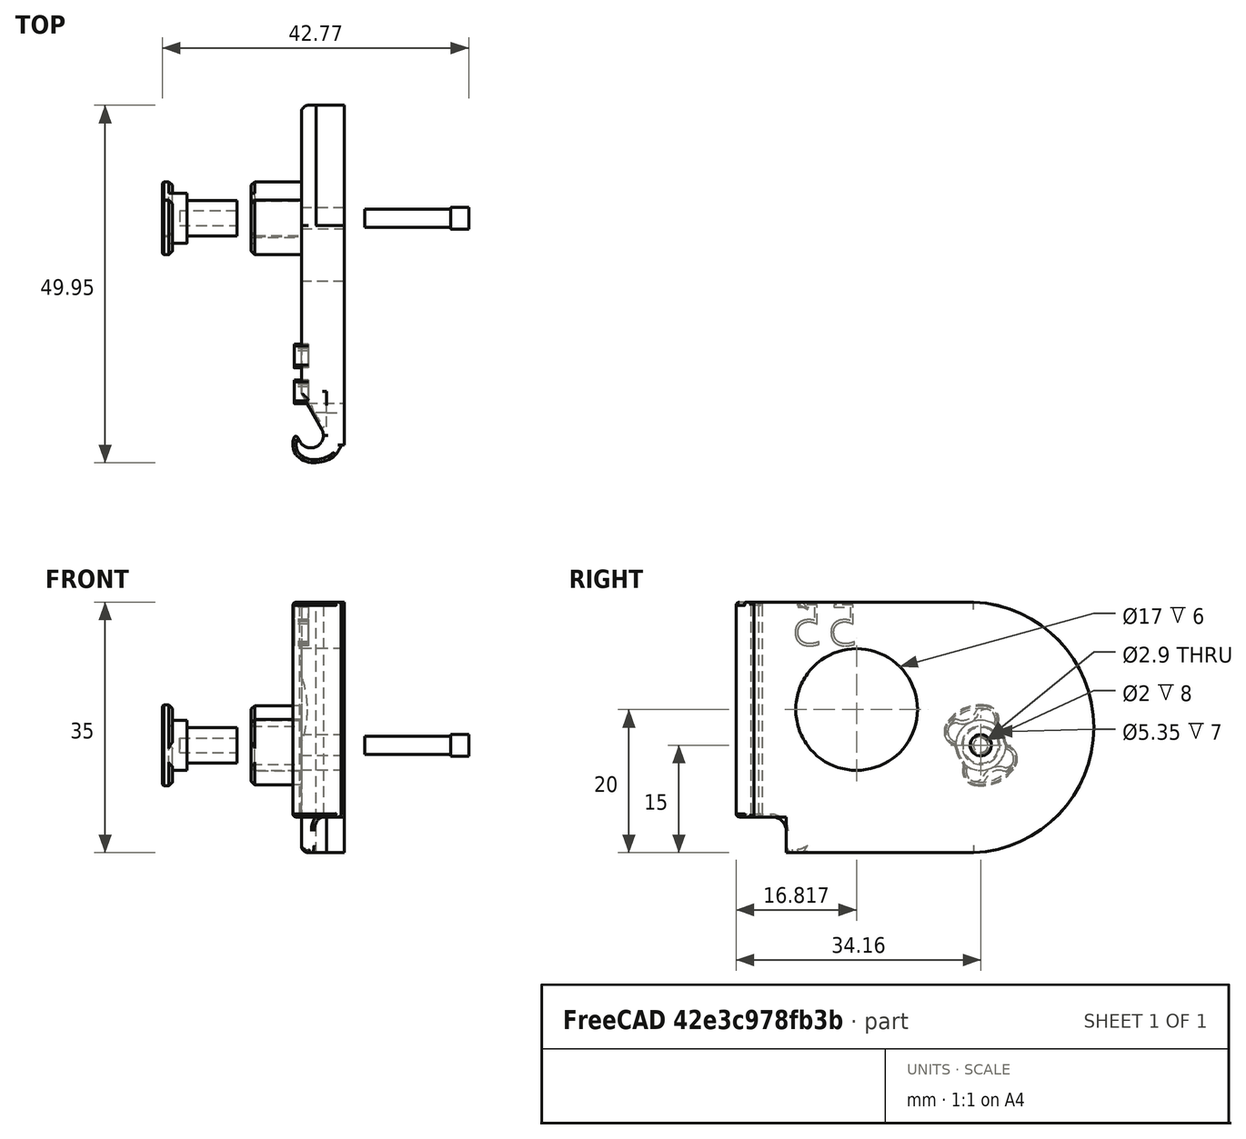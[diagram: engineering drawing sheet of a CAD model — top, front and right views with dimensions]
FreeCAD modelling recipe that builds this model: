
FCSTD DOCUMENT  (FreeCAD 0.18R)
Label: hinge-left-155deg-flat-measurements
License: All rights reserved
LicenseURL: http://en.wikipedia.org/wiki/All_rights_reserved
objects: App::FeaturePython×10, Part::FeaturePython×4, Part::Part2DObjectPython×1, Part::Extrusion×1
note: 6 computed .brp shape members not serialized (recipe doc carries the construction recipe); baked Part::Feature solids carry a one-line shape summary decoded from their .brp

FEATURE [Part::FeaturePython] pillar_base_001  label="pillar-base_001"  # a2plus imported part (geometry in sourceFile) (typed FeaturePython)
  Placement = pos=(0.000603061,0.00261841,-0.00477498) rot=(1,0,0;0.000175rad)
  a2p_Version = V0.1
  fixedPosition = true
  objectType = a2pPart
  sourceFile = ./parts/pillar-base.fcstd
  subassemblyImport = false
  timeLastImport = 1.60452e+09
  updateColors = true
FEATURE [Part::Part2DObjectPython] ShapeString  # Draft 2D object (typed FeaturePython)
  FontFile = <path>
  Placement = pos=(1.61,10.5,29) rot=(0.57735,-0.57735,-0.57735;2.0944rad)
  Size = 6
  String = 55
  Tracking = 0
FEATURE [Part::Extrusion] Extrude
  Base = -> ShapeString
  Dir = (-1,-1e-16,2e-16)
  DirMode = 2
  FaceMakerClass = Part::FaceMakerBullseye
  LengthFwd = 2
  LengthRev = 0
  Solid = false
  Symmetric = false
FEATURE [Part::FeaturePython] bracket_left_flat_001  label="bracket-left-flat_001"  # a2plus imported part (geometry in sourceFile) (typed FeaturePython)
  a2p_Version = V0.1
  fixedPosition = true
  objectType = a2pPart
  sourceFile = ./parts/bracket-left-flat.fcstd
  subassemblyImport = false
  timeLastImport = 1.60454e+09
  updateColors = true
FEATURE [App::FeaturePython] axisCoincident_001  label="axisCoincident_001__bracket-left-flat_001"  # a2plus constraint (typed FeaturePython)
  Object1 = pillar_base_001
  Object2 = bracket_left_flat_001
  ParentTreeObject = -> pillar_base_001
  SubElement1 = Face17
  SubElement2 = Face48
  Suppressed = false
  Type = axial
  directionConstraint = 1
  lockRotation = false
FEATURE [App::FeaturePython] axisCoincident_001_mirror  label="axisCoincident_001__pillar-base_001"  # a2plus constraint (typed FeaturePython)
  Object1 = pillar_base_001
  Object2 = bracket_left_flat_001
  ParentTreeObject = -> bracket_left_flat_001
  SubElement1 = Face17
  SubElement2 = Face48
  Suppressed = false
  Type = axial
  directionConstraint = 1
  lockRotation = false
FEATURE [App::FeaturePython] planeCoincident_001  label="planeCoincident_001__bracket-left-flat_001"  # a2plus constraint (typed FeaturePython)
  Object1 = pillar_base_001
  Object2 = bracket_left_flat_001
  ParentTreeObject = -> pillar_base_001
  SubElement1 = Face1
  SubElement2 = Face72
  Suppressed = false
  Type = plane
  directionConstraint = 0
  offset = 0
FEATURE [App::FeaturePython] planeCoincident_001_mirror  label="planeCoincident_001__pillar-base_001"  # a2plus constraint (typed FeaturePython)
  Object1 = pillar_base_001
  Object2 = bracket_left_flat_001
  ParentTreeObject = -> bracket_left_flat_001
  SubElement1 = Face1
  SubElement2 = Face72
  Suppressed = false
  Type = plane
  directionConstraint = 0
  offset = 0
FEATURE [Part::FeaturePython] pillar_post_001  label="pillar-post_001"  # a2plus imported part (geometry in sourceFile) (typed FeaturePython)
  Placement = pos=(-8.9994,1.6285e-12,-8.2e-15) rot=(0,0,1;0rad)
  a2p_Version = V0.1
  fixedPosition = false
  objectType = a2pPart
  sourceFile = ./parts/pillar-post.fcstd
  subassemblyImport = false
  timeLastImport = 1.60452e+09
  updateColors = true
FEATURE [App::FeaturePython] axisCoincident_002  label="axisCoincident_002__pillar-base_001"  # a2plus constraint (typed FeaturePython)
  Object1 = pillar_post_001
  Object2 = pillar_base_001
  ParentTreeObject = -> pillar_post_001
  SubElement1 = Face32
  SubElement2 = Face17
  Suppressed = false
  Type = axial
  directionConstraint = 0
  lockRotation = false
FEATURE [App::FeaturePython] axisCoincident_002_mirror  label="axisCoincident_002__pillar-post_001"  # a2plus constraint (typed FeaturePython)
  Object1 = pillar_post_001
  Object2 = pillar_base_001
  ParentTreeObject = -> pillar_base_001
  SubElement1 = Face32
  SubElement2 = Face17
  Suppressed = false
  Type = axial
  directionConstraint = 0
  lockRotation = false
FEATURE [App::FeaturePython] planeCoincident_002  label="planeCoincident_002__pillar-base_001"  # a2plus constraint (typed FeaturePython)
  Object1 = pillar_post_001
  Object2 = pillar_base_001
  ParentTreeObject = -> pillar_post_001
  SubElement1 = Face15
  SubElement2 = Face28
  Suppressed = false
  Type = plane
  directionConstraint = 0
  offset = 0
FEATURE [App::FeaturePython] planeCoincident_002_mirror  label="planeCoincident_002__pillar-post_001"  # a2plus constraint (typed FeaturePython)
  Object1 = pillar_post_001
  Object2 = pillar_base_001
  ParentTreeObject = -> pillar_base_001
  SubElement1 = Face15
  SubElement2 = Face28
  Suppressed = false
  Type = plane
  directionConstraint = 0
  offset = 0
FEATURE [Part::FeaturePython] M2_5x12mm_worstCase_001  label="M2.5x12mm-worstCase_001"  # a2plus imported part (geometry in sourceFile) (typed FeaturePython)
  Placement = pos=(21.4763,27.3599,15) rot=(0,-1,0;1.5708rad)
  a2p_Version = V0.1
  fixedPosition = false
  objectType = a2pPart
  sourceFile = ./parts/9000-Miscellaneous/9090z-Screws-Bolts/M2.5x12mm-worstCase.fcstd
  subassemblyImport = false
  timeLastImport = 1.60487e+09
  updateColors = true
FEATURE [App::FeaturePython] axisCoincident_003  label="axisCoincident_003__bracket-left-flat_001"  # a2plus constraint (typed FeaturePython)
  Object1 = M2_5x12mm_worstCase_001
  Object2 = bracket_left_flat_001
  ParentTreeObject = -> M2_5x12mm_worstCase_001
  SubElement1 = Face4
  SubElement2 = Face48
  Suppressed = false
  Type = axial
  directionConstraint = 1
  lockRotation = false
FEATURE [App::FeaturePython] axisCoincident_003_mirror  label="axisCoincident_003__M2.5x12mm-worstCase_001"  # a2plus constraint (typed FeaturePython)
  Object1 = M2_5x12mm_worstCase_001
  Object2 = bracket_left_flat_001
  ParentTreeObject = -> bracket_left_flat_001
  SubElement1 = Face4
  SubElement2 = Face48
  Suppressed = false
  Type = axial
  directionConstraint = 1
  lockRotation = false
note: 1 file-system path scrubbed to <path> (originals preserved in the JSON sidecar)
